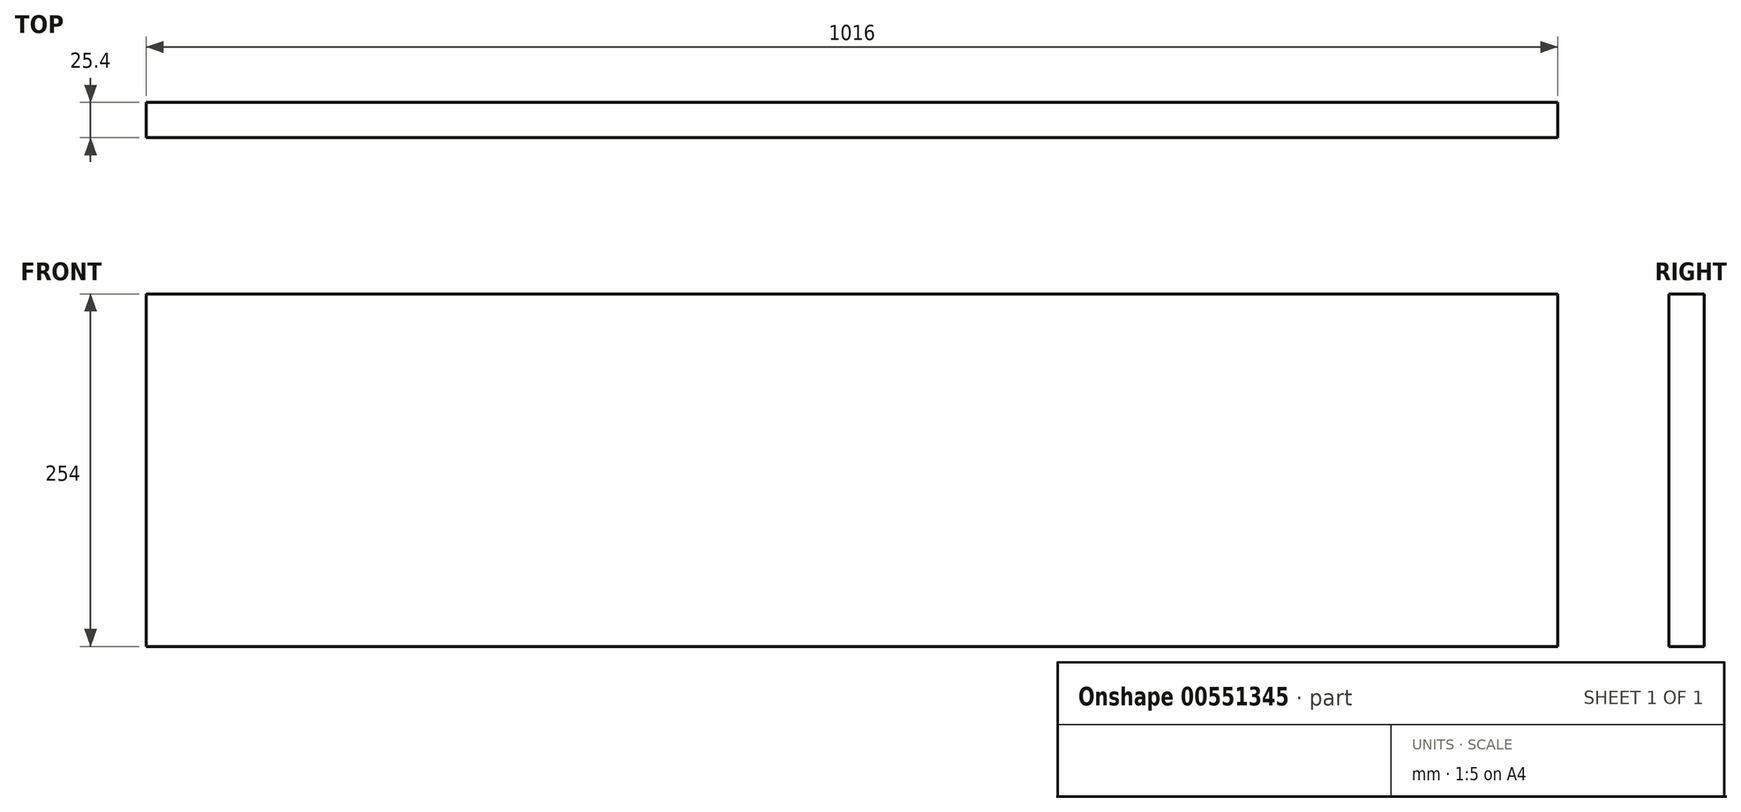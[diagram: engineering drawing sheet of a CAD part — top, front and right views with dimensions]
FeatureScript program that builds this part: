
annotation { "Feature Type Name" : "Feature", "Feature Type Description" : "" }
export const myFeature = defineFeature(function(context is Context, id is Id, definition is map)
    precondition{}
    {
        {
            var Q0;
            Q0=qCreatedBy(makeId("Front.planeOp"),FACE);
            var sketch = newSketch(context, id + "F0", { "sketchPlane" : qUnion([Q0])});
            skLineSegment(sketch, "E0.bottom", {"start": v(508, 127) * mm, "end": v(-508, 127) * mm});
            skLineSegment(sketch, "E0.top", {"start": v(508, -127) * mm, "end": v(-508, -127) * mm});
            skLineSegment(sketch, "E0.left", {"start": v(508, 127) * mm, "end": v(508, -127) * mm});
            skLineSegment(sketch, "E0.right", {"start": v(-508, 127) * mm, "end": v(-508, -127) * mm});
            skPoint(sketch, "E0.middle", {"position": v(0, 0) * mm});
            skSolve(sketch);
        }
        {
            var Q0;
            Q0=makeQuery(id+"F0.imprint","IMPRINT",FACE,{"disambiguationData":[TD([[makeQuery(id+"F0.imprint","IMPRINT",EDGE,{"derivedFrom":sQuery(id+"F0.wireOp",EDGE,"E0.bottom")}),1.0]])]});
            extrude(context, id + "F1", {"entities" : qUnion([Q0]), "depth" : 25.4 * mm, "offsetDistance" : 25.4 * mm});
        }
    });
